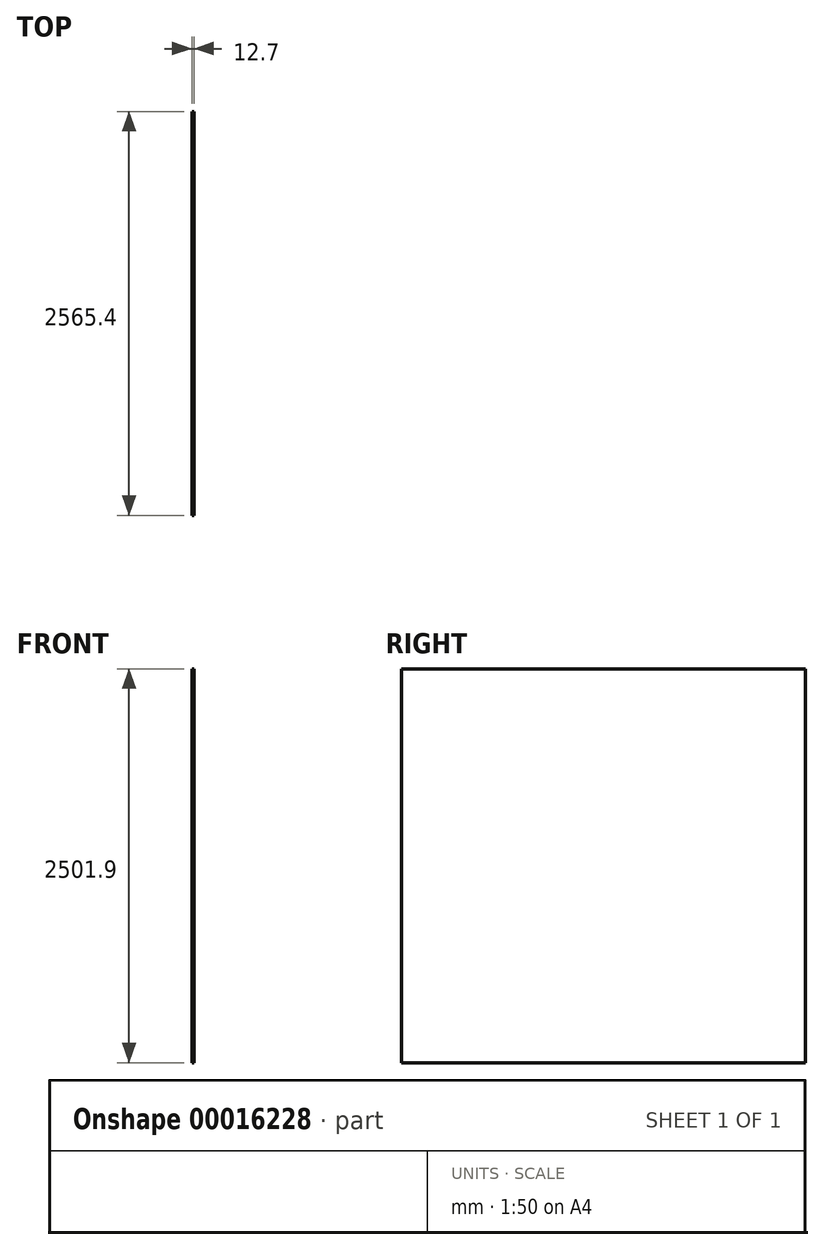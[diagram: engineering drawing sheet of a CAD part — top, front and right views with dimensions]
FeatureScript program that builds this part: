
annotation { "Feature Type Name" : "Feature", "Feature Type Description" : "" }
export const myFeature = defineFeature(function(context is Context, id is Id, definition is map)
    precondition{}
    {
        {
            var Q0;
            Q0=qCreatedBy(makeId("Right.planeOp"),FACE);
            var sketch = newSketch(context, id + "F0", { "sketchPlane" : qUnion([Q0])});
            skLineSegment(sketch, "E0.bottom", {"start": v(-1282.7, 1250.95) * mm, "end": v(1282.7, 1250.95) * mm});
            skLineSegment(sketch, "E0.top", {"start": v(-1282.7, -1250.95) * mm, "end": v(1282.7, -1250.95) * mm});
            skLineSegment(sketch, "E0.left", {"start": v(-1282.7, 1250.95) * mm, "end": v(-1282.7, -1250.95) * mm});
            skLineSegment(sketch, "E0.right", {"start": v(1282.7, 1250.95) * mm, "end": v(1282.7, -1250.95) * mm});
            skPoint(sketch, "E1", {"position": v(1282.7, 0) * mm});
            skPoint(sketch, "E2", {"position": v(0, 1250.95) * mm});
            skSolve(sketch);
        }
        {
            var Q0;
            Q0=makeQuery(id+"F0.imprint","IMPRINT",FACE,{"disambiguationData":[TD([[makeQuery(id+"F0.imprint","IMPRINT",EDGE,{"derivedFrom":sQuery(id+"F0.wireOp",EDGE,"E0.bottom")}),-1.0]])]});
            extrude(context, id + "F1", {"entities" : qUnion([Q0]), "depth" : 12.7 * mm});
        }
    });
